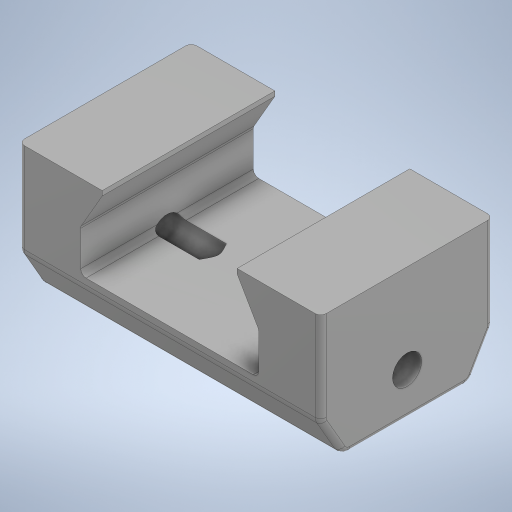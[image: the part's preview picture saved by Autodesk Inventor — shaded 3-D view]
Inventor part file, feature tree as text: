
AUTODESK INVENTOR PART (.ipt)
format: ipt  version: 2023.1 (Build 271208000, 208)  size: 285,184 bytes
history: native  units: mm
features: other x1, fillet x1
ambient origin geometry x8: Origin, YZ Plane, XZ Plane, XY Plane, X Axis, Y Axis, Z Axis, Center Point
bodies: Solid1 (feature_tree)
feature tree (2):
  other  "39300C_TXM-Linear Slide Bushing.STEP"
  fillet  "Fillet5"  [1 undecoded]
note: 1 required parameter value undecoded (feature->parameter linkage not recoverable at this tier; creation-order binding heuristic only, values carry confidence <= 0.55)
